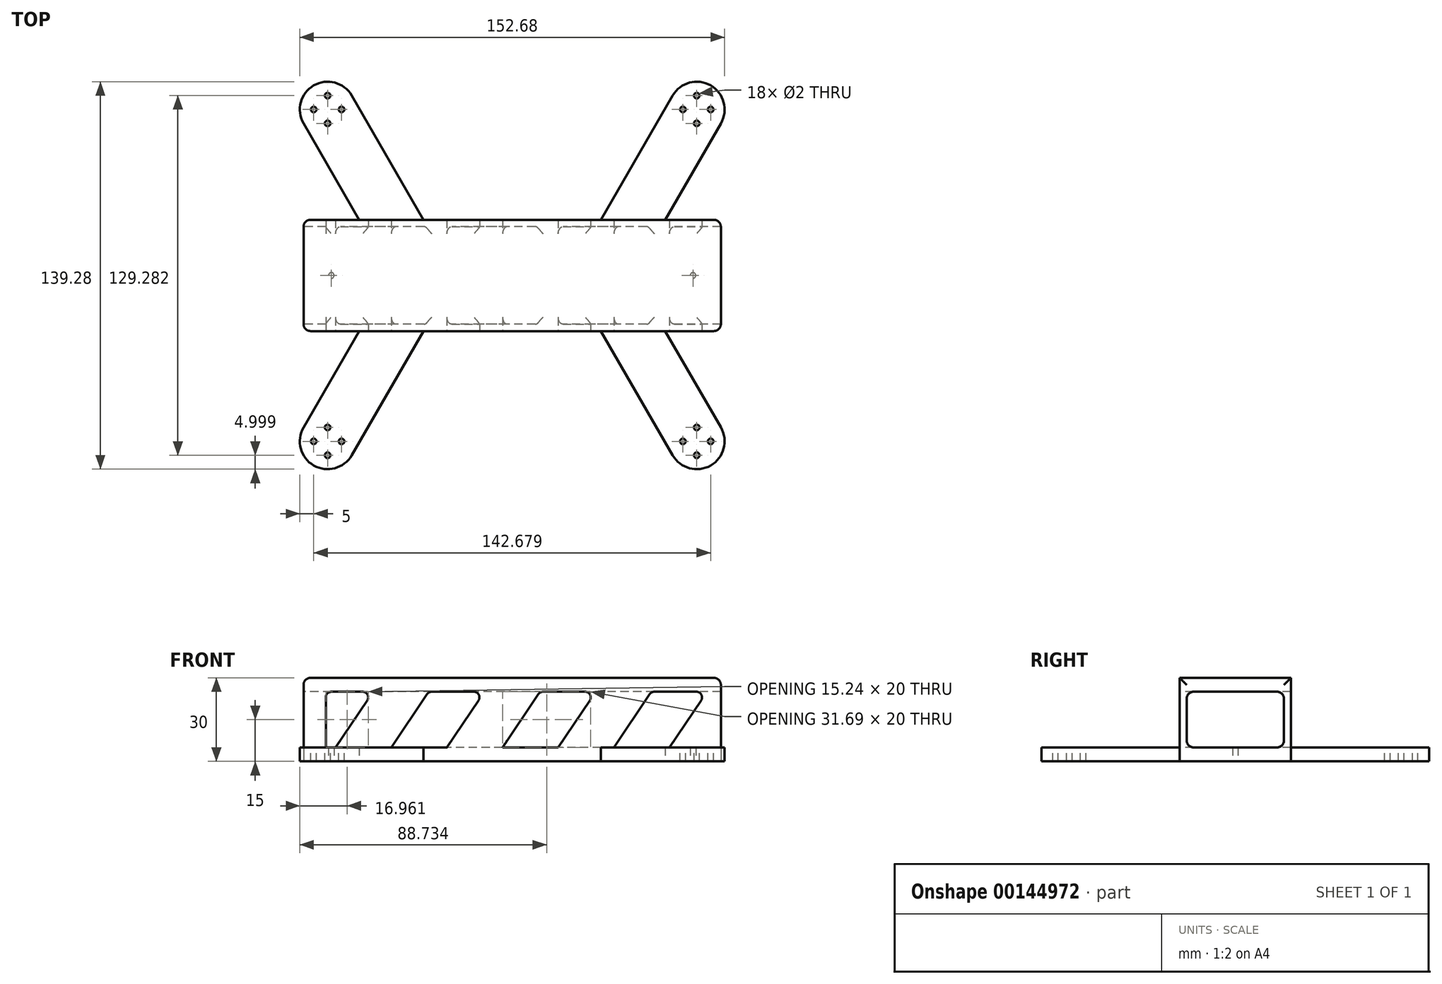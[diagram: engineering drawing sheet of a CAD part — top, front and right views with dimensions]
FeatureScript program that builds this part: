
annotation { "Feature Type Name" : "Feature", "Feature Type Description" : "" }
export const myFeature = defineFeature(function(context is Context, id is Id, definition is map)
    precondition{}
    {
        {
            var Q0;
            Q0=qCreatedBy(makeId("Top.planeOp"),FACE);
            var sketch = newSketch(context, id + "F0", { "sketchPlane" : qUnion([Q0])});
            skLineSegment(sketch, "E0.bottom", {"start": v(75, 20) * mm, "end": v(-75, 20) * mm});
            skLineSegment(sketch, "E0.top", {"start": v(75, -20) * mm, "end": v(-75, -20) * mm});
            skLineSegment(sketch, "E0.left", {"start": v(75, 20) * mm, "end": v(75, -20) * mm});
            skLineSegment(sketch, "E0.right", {"start": v(-75, 20) * mm, "end": v(-75, -20) * mm});
            skPoint(sketch, "E0.middle", {"position": v(0, 0) * mm});
            skLineSegment(sketch, "E1", {"start": v(-55, 20) * mm, "end": v(-75, 54.64) * mm});
            skLineSegment(sketch, "E2", {"start": v(-75, 54.64) * mm, "end": v(-57.68, 64.64) * mm});
            skLineSegment(sketch, "E3", {"start": v(-57.68, 64.64) * mm, "end": v(-31.9, 20) * mm});
            skLineSegment(sketch, "E4", {"start": v(-55, -20) * mm, "end": v(-75, -54.64) * mm});
            skLineSegment(sketch, "E5", {"start": v(-75, -54.64) * mm, "end": v(-57.68, -64.64) * mm});
            skLineSegment(sketch, "E6", {"start": v(-57.68, -64.64) * mm, "end": v(-31.9, -20) * mm});
            skLineSegment(sketch, "E7", {"start": v(-31.9, -20) * mm, "end": v(-55, -20) * mm});
            skLineSegment(sketch, "E8", {"start": v(55, 20) * mm, "end": v(75, 54.64) * mm});
            skLineSegment(sketch, "E9", {"start": v(75, 54.64) * mm, "end": v(57.68, 64.64) * mm});
            skLineSegment(sketch, "E10", {"start": v(57.68, 64.64) * mm, "end": v(31.9, 20) * mm});
            skLineSegment(sketch, "E11", {"start": v(31.9, 20) * mm, "end": v(55, 20) * mm});
            skLineSegment(sketch, "E12", {"start": v(31.9, -20) * mm, "end": v(57.68, -64.64) * mm});
            skLineSegment(sketch, "E13", {"start": v(57.68, -64.64) * mm, "end": v(75, -54.64) * mm});
            skLineSegment(sketch, "E14", {"start": v(75, -54.64) * mm, "end": v(55, -20) * mm});
            skLineSegment(sketch, "E15", {"start": v(55, -20) * mm, "end": v(31.9, -20) * mm});
            skCircle(sketch, "E16", {"center": v(-66.34, 59.64) * mm, "radius": 10 * mm});
            skCircle(sketch, "E17", {"center": v(66.34, 59.64) * mm, "radius": 10 * mm});
            skCircle(sketch, "E18", {"center": v(66.34, -59.64) * mm, "radius": 10 * mm});
            skCircle(sketch, "E19", {"center": v(-66.34, -59.64) * mm, "radius": 10 * mm});
            skSolve(sketch);
        }
        {
            var Q0;
            Q0 = qSketchRegion(id + "F0", true);
            extrude(context, id + "F1", {"entities" : qUnion([Q0]), "depth" : 30 * mm});
        }
        {
            var Q0;
            Q0=makeQuery(id+"F1.opExtrude","CAP_FACE",FACE,{"disambiguationData":[OSD([sQuery(id+"F0.wireOp",EDGE,"E0.bottom"),sQuery(id+"F0.wireOp",EDGE,"E0.top"),sQuery(id+"F0.wireOp",EDGE,"E0.left"),sQuery(id+"F0.wireOp",EDGE,"E0.right"),sQuery(id+"F0.wireOp",EDGE,"E1"),sQuery(id+"F0.wireOp",EDGE,"E3"),sQuery(id+"F0.wireOp",EDGE,"E4"),sQuery(id+"F0.wireOp",EDGE,"E6"),sQuery(id+"F0.wireOp",EDGE,"E8"),sQuery(id+"F0.wireOp",EDGE,"E10"),sQuery(id+"F0.wireOp",EDGE,"E12"),sQuery(id+"F0.wireOp",EDGE,"E14"),sQuery(id+"F0.wireOp",EDGE,"E16"),sQuery(id+"F0.wireOp",EDGE,"E17"),sQuery(id+"F0.wireOp",EDGE,"E18"),sQuery(id+"F0.wireOp",EDGE,"E19")])],"isStart":false});
            var sketch = newSketch(context, id + "F2", { "sketchPlane" : qUnion([Q0])});
            skLineSegment(sketch, "E20.bottom", {"start": v(-87.07, 20) * mm, "end": v(78.02, 20) * mm});
            skLineSegment(sketch, "E20.top", {"start": v(-87.07, 77.55) * mm, "end": v(78.02, 77.55) * mm});
            skLineSegment(sketch, "E20.left", {"start": v(-87.07, 20) * mm, "end": v(-87.07, 77.55) * mm});
            skLineSegment(sketch, "E20.right", {"start": v(78.02, 20) * mm, "end": v(78.02, 77.55) * mm});
            skLineSegment(sketch, "E21.bottom", {"start": v(-85.74, -20) * mm, "end": v(84, -20) * mm});
            skLineSegment(sketch, "E21.top", {"start": v(-85.74, -78.01) * mm, "end": v(84, -78.01) * mm});
            skLineSegment(sketch, "E21.left", {"start": v(-85.74, -20) * mm, "end": v(-85.74, -78.01) * mm});
            skLineSegment(sketch, "E21.right", {"start": v(84, -20) * mm, "end": v(84, -78.01) * mm});
            skSolve(sketch);
        }
        {
            var Q0;
            Q0 = qSketchRegion(id + "F2", true);
            extrude(context, id + "F3", {"entities" : qUnion([Q0]), "operationType" : NewBodyOperationType.REMOVE, "oppositeDirection" : true, "depth" : 25 * mm});
        }
        {
            var Q0;
            Q0=makeQuery(id+"F1.opExtrude","SWEPT_FACE",FACE,{"disambiguationData":[OSD([sQuery(id+"F0.wireOp",EDGE,"E0.right")])]});
            var sketch = newSketch(context, id + "F4", { "sketchPlane" : qUnion([Q0])});
            skLineSegment(sketch, "E22.bottom", {"start": v(-15, 5) * mm, "end": v(15, 5) * mm});
            skLineSegment(sketch, "E22.top", {"start": v(-15, 25) * mm, "end": v(15, 25) * mm});
            skLineSegment(sketch, "E22.left", {"start": v(-17.5, 7.5) * mm, "end": v(-17.5, 22.5) * mm});
            skLineSegment(sketch, "E22.right", {"start": v(17.5, 7.5) * mm, "end": v(17.5, 22.5) * mm});
            skPoint(sketch, "E22.middle", {"position": v(0, 15) * mm});
            skPoint(sketch, "E23.visualSharp", {"position": v(-17.5, 25) * mm});
            skArc(sketch, "E23.filletArc", {"start": v(-15, 25) * mm, "mid": v(-16.77, 24.27) * mm, "end": v(-17.5, 22.5) * mm});
            skPoint(sketch, "E24.visualSharp", {"position": v(17.5, 25) * mm});
            skArc(sketch, "E24.filletArc", {"start": v(17.5, 22.5) * mm, "mid": v(16.77, 24.27) * mm, "end": v(15, 25) * mm});
            skPoint(sketch, "E25.visualSharp", {"position": v(17.5, 5) * mm});
            skArc(sketch, "E25.filletArc", {"start": v(15, 5) * mm, "mid": v(16.77, 5.73) * mm, "end": v(17.5, 7.5) * mm});
            skPoint(sketch, "E26.visualSharp", {"position": v(-17.5, 5) * mm});
            skArc(sketch, "E26.filletArc", {"start": v(-17.5, 7.5) * mm, "mid": v(-16.77, 5.73) * mm, "end": v(-15, 5) * mm});
            skSolve(sketch);
        }
        {
            var Q0;
            Q0=makeQuery(id+"F4.imprint","IMPRINT",FACE,{"disambiguationData":[TD([[makeQuery(id+"F4.imprint","IMPRINT",EDGE,{"derivedFrom":sQuery(id+"F4.wireOp",EDGE,"E22.bottom")}),1.0]])]});
            extrude(context, id + "F5", {"entities" : qUnion([Q0]), "operationType" : NewBodyOperationType.REMOVE, "endBound" : BoundingType.THROUGH_ALL, "oppositeDirection" : true, "depth" : 140 * mm});
        }
        {
            var Q0;
            {var subQ0=sQuery(id+"F0.wireOp",EDGE,"E0.top");var subQ1=sQuery(id+"F0.wireOp",EDGE,"E7");Q0=makeQuery(id+"F3.boolean.opBoolean","MERGE",FACE,{"derivedFrom":[makeQuery(id+"F1.opExtrude","SWEPT_FACE",FACE,{"disambiguationData":[OSD([subQ0]),TDD([makeQuery(id+"F0.imprint","IMPRINT",EDGE,{"disambiguationData":[TD([[makeQuery(id+"F0.imprint","INTERSECT",VERTEX,{"derivedFrom":[subQ0,sQuery(id+"F0.wireOp",EDGE,"E0.left")]}),-1.0]])],"derivedFrom":subQ0})])]}),makeQuery(id+"F1.opExtrude","SWEPT_FACE",FACE,{"disambiguationData":[OSD([subQ0]),TDD([makeQuery(id+"F0.imprint","IMPRINT",EDGE,{"disambiguationData":[TD([[makeQuery(id+"F0.imprint","INTERSECT",VERTEX,{"derivedFrom":[subQ0,sQuery(id+"F0.wireOp",EDGE,"E6"),subQ1]}),1.0]])],"derivedFrom":subQ0})])]}),makeQuery(id+"F1.opExtrude","SWEPT_FACE",FACE,{"disambiguationData":[OSD([subQ0]),TDD([makeQuery(id+"F0.imprint","IMPRINT",EDGE,{"disambiguationData":[TD([[makeQuery(id+"F0.imprint","INTERSECT",VERTEX,{"derivedFrom":[subQ0,sQuery(id+"F0.wireOp",EDGE,"E0.right")]}),1.0]])],"derivedFrom":subQ0})])]}),makeQuery(id+"F3.opExtrude","SWEPT_FACE",FACE,{"disambiguationData":[OSD([sQuery(id+"F2.wireOp",EDGE,"E21.bottom")])]})]});}
            var sketch = newSketch(context, id + "F6", { "sketchPlane" : qUnion([Q0])});
            skLineSegment(sketch, "E27.bottom", {"start": v(66.24, 25) * mm, "end": v(51.07, 25) * mm});
            skLineSegment(sketch, "E27.top", {"start": v(56.55, 5) * mm, "end": v(36.55, 5) * mm});
            skLineSegment(sketch, "E27.right", {"start": v(-67, 23) * mm, "end": v(-67, 5) * mm});
            skLineSegment(sketch, "E28", {"start": v(-67, 5) * mm, "end": v(-63.45, 5) * mm});
            skLineSegment(sketch, "E29", {"start": v(-63.45, 5) * mm, "end": v(-52.1, 21.88) * mm});
            skLineSegment(sketch, "E30", {"start": v(-30.6, 24.12) * mm, "end": v(-43.45, 5) * mm});
            skLineSegment(sketch, "E31", {"start": v(-43.45, 5) * mm, "end": v(-23.45, 5) * mm});
            skLineSegment(sketch, "E32", {"start": v(-23.45, 5) * mm, "end": v(-12.1, 21.88) * mm});
            skLineSegment(sketch, "E33", {"start": v(9.4, 24.12) * mm, "end": v(-3.45, 5) * mm});
            skLineSegment(sketch, "E34", {"start": v(-3.45, 5) * mm, "end": v(16.55, 5) * mm});
            skLineSegment(sketch, "E35", {"start": v(16.55, 5) * mm, "end": v(27.9, 21.88) * mm});
            skLineSegment(sketch, "E36", {"start": v(49.4, 24.12) * mm, "end": v(36.55, 5) * mm});
            skLineSegment(sketch, "E37", {"start": v(36.55, 5) * mm, "end": v(56.55, 5) * mm});
            skLineSegment(sketch, "E38", {"start": v(56.55, 5) * mm, "end": v(67.9, 21.88) * mm});
            skPoint(sketch, "E39.start.orphan", {"position": v(-70, 25) * mm});
            skLineSegment(sketch, "E40.trimOffspring", {"start": v(-63.45, 5) * mm, "end": v(-67, 5) * mm});
            skLineSegment(sketch, "E41.trimOffspring", {"start": v(-13.76, 25) * mm, "end": v(-28.93, 25) * mm});
            skLineSegment(sketch, "E42.trimOffspring", {"start": v(-23.45, 5) * mm, "end": v(-43.45, 5) * mm});
            skLineSegment(sketch, "E43.trimOffspring", {"start": v(-53.76, 25) * mm, "end": v(-65, 25) * mm});
            skLineSegment(sketch, "E44.trimOffspring", {"start": v(26.24, 25) * mm, "end": v(11.07, 25) * mm});
            skLineSegment(sketch, "E45.trimOffspring", {"start": v(16.55, 5) * mm, "end": v(-3.45, 5) * mm});
            skPoint(sketch, "E46.visualSharp", {"position": v(-67, 25) * mm});
            skArc(sketch, "E46.filletArc", {"start": v(-65, 25) * mm, "mid": v(-66.41, 24.41) * mm, "end": v(-67, 23) * mm});
            skPoint(sketch, "E47.visualSharp", {"position": v(-50, 25) * mm});
            skArc(sketch, "E47.filletArc", {"start": v(-52.1, 21.88) * mm, "mid": v(-52, 23.94) * mm, "end": v(-53.76, 25) * mm});
            skPoint(sketch, "E48.visualSharp", {"position": v(-30, 25) * mm});
            skArc(sketch, "E48.filletArc", {"start": v(-28.93, 25) * mm, "mid": v(-29.88, 24.77) * mm, "end": v(-30.6, 24.12) * mm});
            skPoint(sketch, "E49.visualSharp", {"position": v(-10, 25) * mm});
            skArc(sketch, "E49.filletArc", {"start": v(-12.1, 21.88) * mm, "mid": v(-12, 23.94) * mm, "end": v(-13.76, 25) * mm});
            skPoint(sketch, "E50.visualSharp", {"position": v(10, 25) * mm});
            skArc(sketch, "E50.filletArc", {"start": v(11.07, 25) * mm, "mid": v(10.12, 24.77) * mm, "end": v(9.4, 24.12) * mm});
            skPoint(sketch, "E51.visualSharp", {"position": v(30, 25) * mm});
            skArc(sketch, "E51.filletArc", {"start": v(27.9, 21.88) * mm, "mid": v(28, 23.94) * mm, "end": v(26.24, 25) * mm});
            skPoint(sketch, "E52.visualSharp", {"position": v(50, 25) * mm});
            skArc(sketch, "E52.filletArc", {"start": v(51.07, 25) * mm, "mid": v(50.12, 24.77) * mm, "end": v(49.4, 24.12) * mm});
            skPoint(sketch, "E53.visualSharp", {"position": v(70, 25) * mm});
            skArc(sketch, "E53.filletArc", {"start": v(67.9, 21.88) * mm, "mid": v(68, 23.94) * mm, "end": v(66.24, 25) * mm});
            skSolve(sketch);
        }
        {
            var Q0;
            Q0 = qSketchRegion(id + "F6", true);
            extrude(context, id + "F7", {"entities" : qUnion([Q0]), "operationType" : NewBodyOperationType.REMOVE, "endBound" : BoundingType.THROUGH_ALL, "oppositeDirection" : true, "depth" : 25 * mm});
        }
        {
            var Q0;
            Q0=makeQuery(id+"F1.opExtrude","SWEPT_EDGE",EDGE,{"disambiguationData":[OSD([sQuery(id+"F0.wireOp",EDGE,"E0.top"),sQuery(id+"F0.wireOp",EDGE,"E0.right")])]});
            var Q1;
            {var subQ0=sQuery(id+"F0.wireOp",EDGE,"E0.top");var subQ1=sQuery(id+"F0.wireOp",EDGE,"E7");Q1=makeQuery(id+"F3.boolean.opBoolean","MERGE",EDGE,{"derivedFrom":[makeQuery(id+"F1.opExtrude","CAP_EDGE",EDGE,{"disambiguationData":[OSD([subQ0]),TDD([makeQuery(id+"F0.imprint","IMPRINT",EDGE,{"disambiguationData":[TD([[makeQuery(id+"F0.imprint","INTERSECT",VERTEX,{"derivedFrom":[subQ0,sQuery(id+"F0.wireOp",EDGE,"E0.left")]}),-1.0]])],"derivedFrom":subQ0})])],"isStart":false}),makeQuery(id+"F1.opExtrude","CAP_EDGE",EDGE,{"disambiguationData":[OSD([subQ0]),TDD([makeQuery(id+"F0.imprint","IMPRINT",EDGE,{"disambiguationData":[TD([[makeQuery(id+"F0.imprint","INTERSECT",VERTEX,{"derivedFrom":[subQ0,sQuery(id+"F0.wireOp",EDGE,"E6"),subQ1]}),1.0]])],"derivedFrom":subQ0})])],"isStart":false}),makeQuery(id+"F1.opExtrude","CAP_EDGE",EDGE,{"disambiguationData":[OSD([subQ0]),TDD([makeQuery(id+"F0.imprint","IMPRINT",EDGE,{"disambiguationData":[TD([[makeQuery(id+"F0.imprint","INTERSECT",VERTEX,{"derivedFrom":[subQ0,sQuery(id+"F0.wireOp",EDGE,"E0.right")]}),1.0]])],"derivedFrom":subQ0})])],"isStart":false}),makeQuery(id+"F3.opExtrude","CAP_EDGE",EDGE,{"disambiguationData":[OSD([sQuery(id+"F2.wireOp",EDGE,"E21.bottom")])],"isStart":true})]});}
            var Q2;
            Q2=makeQuery(id+"F1.opExtrude","CAP_EDGE",EDGE,{"disambiguationData":[OSD([sQuery(id+"F0.wireOp",EDGE,"E0.right")])],"isStart":false});
            var Q3;
            Q3=makeQuery(id+"F1.opExtrude","SWEPT_EDGE",EDGE,{"disambiguationData":[OSD([sQuery(id+"F0.wireOp",EDGE,"E0.bottom"),sQuery(id+"F0.wireOp",EDGE,"E0.right")])]});
            var Q4;
            {var subQ0=sQuery(id+"F0.wireOp",EDGE,"E0.bottom");Q4=makeQuery(id+"F3.boolean.opBoolean","MERGE",EDGE,{"derivedFrom":[makeQuery(id+"F1.opExtrude","CAP_EDGE",EDGE,{"disambiguationData":[OSD([subQ0]),TDD([makeQuery(id+"F0.imprint","IMPRINT",EDGE,{"disambiguationData":[TD([[makeQuery(id+"F0.imprint","INTERSECT",VERTEX,{"derivedFrom":[subQ0,sQuery(id+"F0.wireOp",EDGE,"E0.left")]}),-1.0]])],"derivedFrom":subQ0})])],"isStart":false}),makeQuery(id+"F1.opExtrude","CAP_EDGE",EDGE,{"disambiguationData":[OSD([subQ0]),TDD([makeQuery(id+"F0.imprint","IMPRINT",EDGE,{"disambiguationData":[TD([[makeQuery(id+"F0.imprint","INTERSECT",VERTEX,{"derivedFrom":[subQ0,sQuery(id+"F0.wireOp",EDGE,"E3")]}),1.0]])],"derivedFrom":subQ0})])],"isStart":false}),makeQuery(id+"F1.opExtrude","CAP_EDGE",EDGE,{"disambiguationData":[OSD([subQ0]),TDD([makeQuery(id+"F0.imprint","IMPRINT",EDGE,{"disambiguationData":[TD([[makeQuery(id+"F0.imprint","INTERSECT",VERTEX,{"derivedFrom":[subQ0,sQuery(id+"F0.wireOp",EDGE,"E0.right")]}),1.0]])],"derivedFrom":subQ0})])],"isStart":false}),makeQuery(id+"F3.opExtrude","CAP_EDGE",EDGE,{"disambiguationData":[OSD([sQuery(id+"F2.wireOp",EDGE,"E20.bottom")])],"isStart":true})]});}
            var Q5;
            Q5=makeQuery(id+"F1.opExtrude","CAP_EDGE",EDGE,{"disambiguationData":[OSD([sQuery(id+"F0.wireOp",EDGE,"E0.left")])],"isStart":false});
            var Q6;
            Q6=makeQuery(id+"F1.opExtrude","SWEPT_EDGE",EDGE,{"disambiguationData":[OSD([sQuery(id+"F0.wireOp",EDGE,"E0.top"),sQuery(id+"F0.wireOp",EDGE,"E0.left")])]});
            var Q7;
            Q7=makeQuery(id+"F1.opExtrude","SWEPT_EDGE",EDGE,{"disambiguationData":[OSD([sQuery(id+"F0.wireOp",EDGE,"E0.bottom"),sQuery(id+"F0.wireOp",EDGE,"E0.left")])]});
            fillet(context, id + "F8", {"entities" : qUnion([Q0, Q1, Q2, Q3, Q4, Q5, Q6, Q7]), "radius" : 2.5 * mm, "tangentPropagation" : true, "allowEdgeOverflow" : false});
        }
        {
            var Q0;
            {var subQ0=makeQuery(id+"F3.opExtrude","CAP_FACE",FACE,{"disambiguationData":[OSD([sQuery(id+"F2.wireOp",EDGE,"E21.bottom"),sQuery(id+"F2.wireOp",EDGE,"E21.top"),sQuery(id+"F2.wireOp",EDGE,"E21.left"),sQuery(id+"F2.wireOp",EDGE,"E21.right")])],"isStart":false});var subQ1=makeQuery(id+"F3.opExtrude","CAP_FACE",FACE,{"disambiguationData":[OSD([sQuery(id+"F2.wireOp",EDGE,"E20.bottom"),sQuery(id+"F2.wireOp",EDGE,"E20.top"),sQuery(id+"F2.wireOp",EDGE,"E20.left"),sQuery(id+"F2.wireOp",EDGE,"E20.right")])],"isStart":false});Q0=makeQuery(id+"F7.boolean.opBoolean","MERGE",FACE,{"derivedFrom":[makeQuery(id+"F3.boolean.opBoolean","COPY",FACE,{"disambiguationData":[OD(0.0)],"derivedFrom":subQ1}),makeQuery(id+"F3.boolean.opBoolean","COPY",FACE,{"disambiguationData":[OD(1.0)],"derivedFrom":subQ1}),makeQuery(id+"F3.boolean.opBoolean","COPY",FACE,{"disambiguationData":[OD(0.0)],"derivedFrom":subQ0}),makeQuery(id+"F3.boolean.opBoolean","COPY",FACE,{"disambiguationData":[OD(1.0)],"derivedFrom":subQ0}),makeQuery(id+"F5.boolean.opBoolean","COPY",FACE,{"derivedFrom":makeQuery(id+"F5.opExtrude","SWEPT_FACE",FACE,{"disambiguationData":[OSD([sQuery(id+"F4.wireOp",EDGE,"E22.bottom")])]})}),makeQuery(id+"F7.opExtrude","SWEPT_FACE",FACE,{"disambiguationData":[OSD([sQuery(id+"F6.wireOp",EDGE,"E37")])]}),makeQuery(id+"F7.opExtrude","SWEPT_FACE",FACE,{"disambiguationData":[OSD([sQuery(id+"F6.wireOp",EDGE,"E40.trimOffspring")])]}),makeQuery(id+"F7.opExtrude","SWEPT_FACE",FACE,{"disambiguationData":[OSD([sQuery(id+"F6.wireOp",EDGE,"E42.trimOffspring")])]}),makeQuery(id+"F7.opExtrude","SWEPT_FACE",FACE,{"disambiguationData":[OSD([sQuery(id+"F6.wireOp",EDGE,"E45.trimOffspring")])]})]});}
            var sketch = newSketch(context, id + "F9", { "sketchPlane" : qUnion([Q0])});
            skCircle(sketch, "E54", {"center": v(-66.34, 54.64) * mm, "radius": 1 * mm});
            skCircle(sketch, "E55", {"center": v(-66.34, 64.64) * mm, "radius": 1 * mm});
            skCircle(sketch, "E56", {"center": v(66.34, 64.64) * mm, "radius": 1 * mm});
            skCircle(sketch, "E57", {"center": v(66.34, 54.64) * mm, "radius": 1 * mm});
            skCircle(sketch, "E58", {"center": v(-66.34, -54.64) * mm, "radius": 1 * mm});
            skCircle(sketch, "E59", {"center": v(-66.34, -64.64) * mm, "radius": 1 * mm});
            skCircle(sketch, "E60", {"center": v(-71.34, 59.64) * mm, "radius": 1 * mm});
            skCircle(sketch, "E61", {"center": v(-61.34, 59.64) * mm, "radius": 1 * mm});
            skCircle(sketch, "E62.MirrorC", {"center": v(71.34, 59.64) * mm, "radius": 1 * mm});
            skCircle(sketch, "E63.MirrorC", {"center": v(61.34, 59.64) * mm, "radius": 1 * mm});
            skCircle(sketch, "E64.MirrorC", {"center": v(-61.34, -59.64) * mm, "radius": 1 * mm});
            skCircle(sketch, "E65.MirrorC", {"center": v(-71.34, -59.64) * mm, "radius": 1 * mm});
            skCircle(sketch, "E66.MirrorC", {"center": v(66.34, -54.64) * mm, "radius": 1 * mm});
            skCircle(sketch, "E67.MirrorC", {"center": v(66.34, -64.64) * mm, "radius": 1 * mm});
            skCircle(sketch, "E68.MirrorC", {"center": v(71.34, -59.64) * mm, "radius": 1 * mm});
            skCircle(sketch, "E69.MirrorC", {"center": v(61.34, -59.64) * mm, "radius": 1 * mm});
            skSolve(sketch);
        }
        {
            var Q0;
            Q0 = qSketchRegion(id + "F9", true);
            extrude(context, id + "F10", {"entities" : qUnion([Q0]), "operationType" : NewBodyOperationType.REMOVE, "endBound" : BoundingType.THROUGH_ALL, "oppositeDirection" : true, "depth" : 25 * mm});
        }
        {
            var Q0;
            Q0=makeQuery(id+"F1.opExtrude","CAP_FACE",FACE,{"disambiguationData":[OSD([sQuery(id+"F0.wireOp",EDGE,"E0.bottom"),sQuery(id+"F0.wireOp",EDGE,"E0.top"),sQuery(id+"F0.wireOp",EDGE,"E0.left"),sQuery(id+"F0.wireOp",EDGE,"E0.right"),sQuery(id+"F0.wireOp",EDGE,"E1"),sQuery(id+"F0.wireOp",EDGE,"E3"),sQuery(id+"F0.wireOp",EDGE,"E4"),sQuery(id+"F0.wireOp",EDGE,"E6"),sQuery(id+"F0.wireOp",EDGE,"E8"),sQuery(id+"F0.wireOp",EDGE,"E10"),sQuery(id+"F0.wireOp",EDGE,"E12"),sQuery(id+"F0.wireOp",EDGE,"E14"),sQuery(id+"F0.wireOp",EDGE,"E16"),sQuery(id+"F0.wireOp",EDGE,"E17"),sQuery(id+"F0.wireOp",EDGE,"E18"),sQuery(id+"F0.wireOp",EDGE,"E19")])],"isStart":true});
            var sketch = newSketch(context, id + "F11", { "sketchPlane" : qUnion([Q0])});
            skCircle(sketch, "E70", {"center": v(-65, 0) * mm, "radius": 1 * mm});
            skCircle(sketch, "E71", {"center": v(65, 0) * mm, "radius": 1 * mm});
            skSolve(sketch);
        }
        {
            var Q0;
            Q0=makeQuery(id+"F11.imprint","IMPRINT",FACE,{"disambiguationData":[TD([[makeQuery(id+"F11.imprint","IMPRINT",EDGE,{"derivedFrom":sQuery(id+"F11.wireOp",EDGE,"E70")}),1.0]])]});
            var Q1;
            Q1=makeQuery(id+"F11.imprint","IMPRINT",FACE,{"disambiguationData":[TD([[makeQuery(id+"F11.imprint","IMPRINT",EDGE,{"derivedFrom":sQuery(id+"F11.wireOp",EDGE,"E71")}),1.0]])]});
            var Q2;
            Q2=sQuery(id+"F11.wireOp",EDGE,"E70");
            var Q3;
            Q3=sQuery(id+"F11.wireOp",EDGE,"E71");
            extrude(context, id + "F12", {"entities" : qUnion([Q0, Q1]), "operationType" : NewBodyOperationType.REMOVE, "surfaceEntities" : qUnion([Q2, Q3]), "oppositeDirection" : true, "depth" : 5 * mm});
        }
    });
